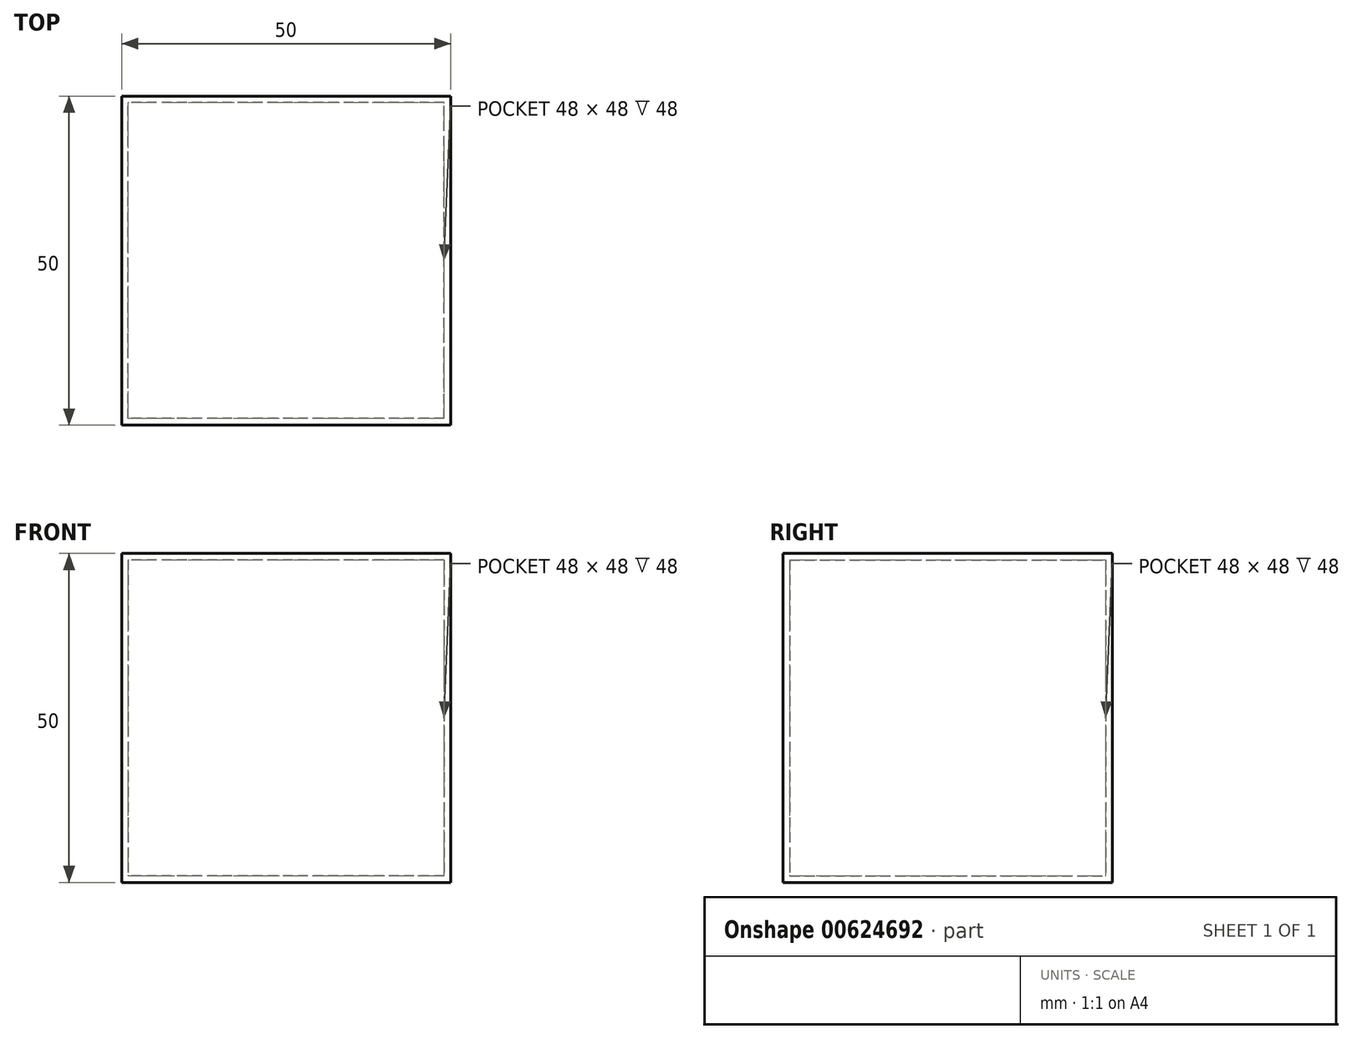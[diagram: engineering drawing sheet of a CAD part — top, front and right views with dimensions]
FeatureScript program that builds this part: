
annotation { "Feature Type Name" : "Feature", "Feature Type Description" : "" }
export const myFeature = defineFeature(function(context is Context, id is Id, definition is map)
    precondition{}
    {
        {
            var Q0;
            Q0=qCreatedBy(makeId("Front.planeOp"),FACE);
            var sketch = newSketch(context, id + "F0", { "sketchPlane" : qUnion([Q0])});
            skLineSegment(sketch, "E0.bottom", {"start": v(25, 25) * mm, "end": v(-25, 25) * mm});
            skLineSegment(sketch, "E0.top", {"start": v(25, -25) * mm, "end": v(-25, -25) * mm});
            skLineSegment(sketch, "E0.left", {"start": v(25, 25) * mm, "end": v(25, -25) * mm});
            skLineSegment(sketch, "E0.right", {"start": v(-25, 25) * mm, "end": v(-25, -25) * mm});
            skPoint(sketch, "E0.middle", {"position": v(0, 0) * mm});
            skLineSegment(sketch, "E1.bottom", {"start": v(24, 24) * mm, "end": v(-24, 24) * mm});
            skLineSegment(sketch, "E1.top", {"start": v(24, -24) * mm, "end": v(-24, -24) * mm});
            skLineSegment(sketch, "E1.left", {"start": v(24, 24) * mm, "end": v(24, -24) * mm});
            skLineSegment(sketch, "E1.right", {"start": v(-24, 24) * mm, "end": v(-24, -24) * mm});
            skSolve(sketch);
        }
        {
            var Q0;
            Q0=makeQuery(id+"F0.imprint","IMPRINT",FACE,{"disambiguationData":[TD([[makeQuery(id+"F0.imprint","IMPRINT",EDGE,{"derivedFrom":sQuery(id+"F0.wireOp",EDGE,"E0.bottom")}),1.0]])]});
            var Q1;
            Q1=makeQuery(id+"F0.imprint","IMPRINT",FACE,{"disambiguationData":[TD([[makeQuery(id+"F0.imprint","IMPRINT",EDGE,{"derivedFrom":sQuery(id+"F0.wireOp",EDGE,"E1.bottom")}),1.0]])]});
            extrude(context, id + "F1", {"entities" : qUnion([Q0, Q1]), "depth" : 50 * mm, "offsetDistance" : 25 * mm, "symmetric" : true});
        }
        {
            var Q0;
            Q0=makeQuery(id+"F0.imprint","IMPRINT",FACE,{"disambiguationData":[TD([[makeQuery(id+"F0.imprint","IMPRINT",EDGE,{"derivedFrom":sQuery(id+"F0.wireOp",EDGE,"E1.bottom")}),1.0]])]});
            extrude(context, id + "F2", {"entities" : qUnion([Q0]), "depth" : 48 * mm, "offsetDistance" : 25 * mm, "symmetric" : true});
        }
        {
            var Q0;
            Q0=makeQuery(id+"F2.opExtrude","SWEPT_BODY",BODY,{"disambiguationData":[OSD([sQuery(id+"F0.wireOp",EDGE,"E1.bottom"),sQuery(id+"F0.wireOp",EDGE,"E1.top"),sQuery(id+"F0.wireOp",EDGE,"E1.left"),sQuery(id+"F0.wireOp",EDGE,"E1.right")])]});
            var Q1;
            Q1=makeQuery(id+"F1.opExtrude","SWEPT_BODY",BODY,{"disambiguationData":[OSD([sQuery(id+"F0.wireOp",EDGE,"E0.bottom"),sQuery(id+"F0.wireOp",EDGE,"E0.top"),sQuery(id+"F0.wireOp",EDGE,"E0.left"),sQuery(id+"F0.wireOp",EDGE,"E0.right")])]});
            booleanBodies(context, id + "F3", {"operationType" : BooleanOperationType.SUBTRACTION, "tools" : qUnion([Q0]), "targets" : qUnion([Q1])});
        }
    });
